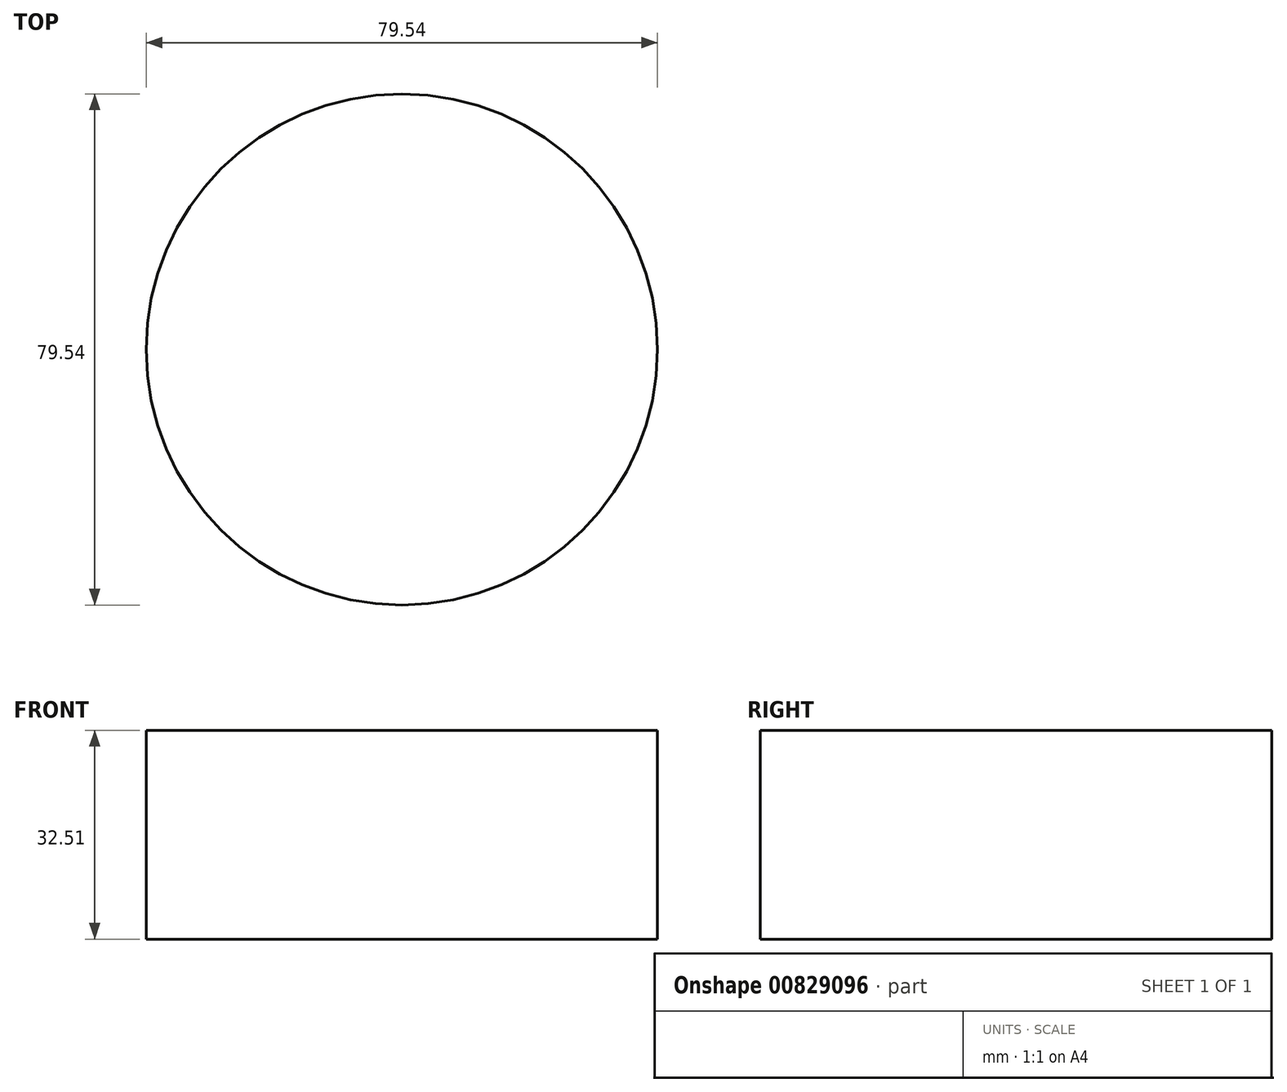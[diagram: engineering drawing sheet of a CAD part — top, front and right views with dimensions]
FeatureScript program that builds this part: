
annotation { "Feature Type Name" : "Feature", "Feature Type Description" : "" }
export const myFeature = defineFeature(function(context is Context, id is Id, definition is map)
    precondition{}
    {
        {
            var Q0;
            Q0=qCreatedBy(makeId("Top.planeOp"),FACE);
            var sketch = newSketch(context, id + "F0", { "sketchPlane" : qUnion([Q0])});
            skCircle(sketch, "E0", {"center": v(64.02, -46.01) * mm, "radius": 39.77 * mm});
            skSolve(sketch);
        }
        {
            var Q0;
            Q0=makeQuery(id+"F0.imprint","IMPRINT",FACE,{"disambiguationData":[TD([[makeQuery(id+"F0.imprint","IMPRINT",EDGE,{"derivedFrom":sQuery(id+"F0.wireOp",EDGE,"E0")}),1.0]])]});
            extrude(context, id + "F1", {"entities" : qUnion([Q0]), "depth" : 32.5 * mm, "offsetDistance" : 25.4 * mm});
        }
    });
